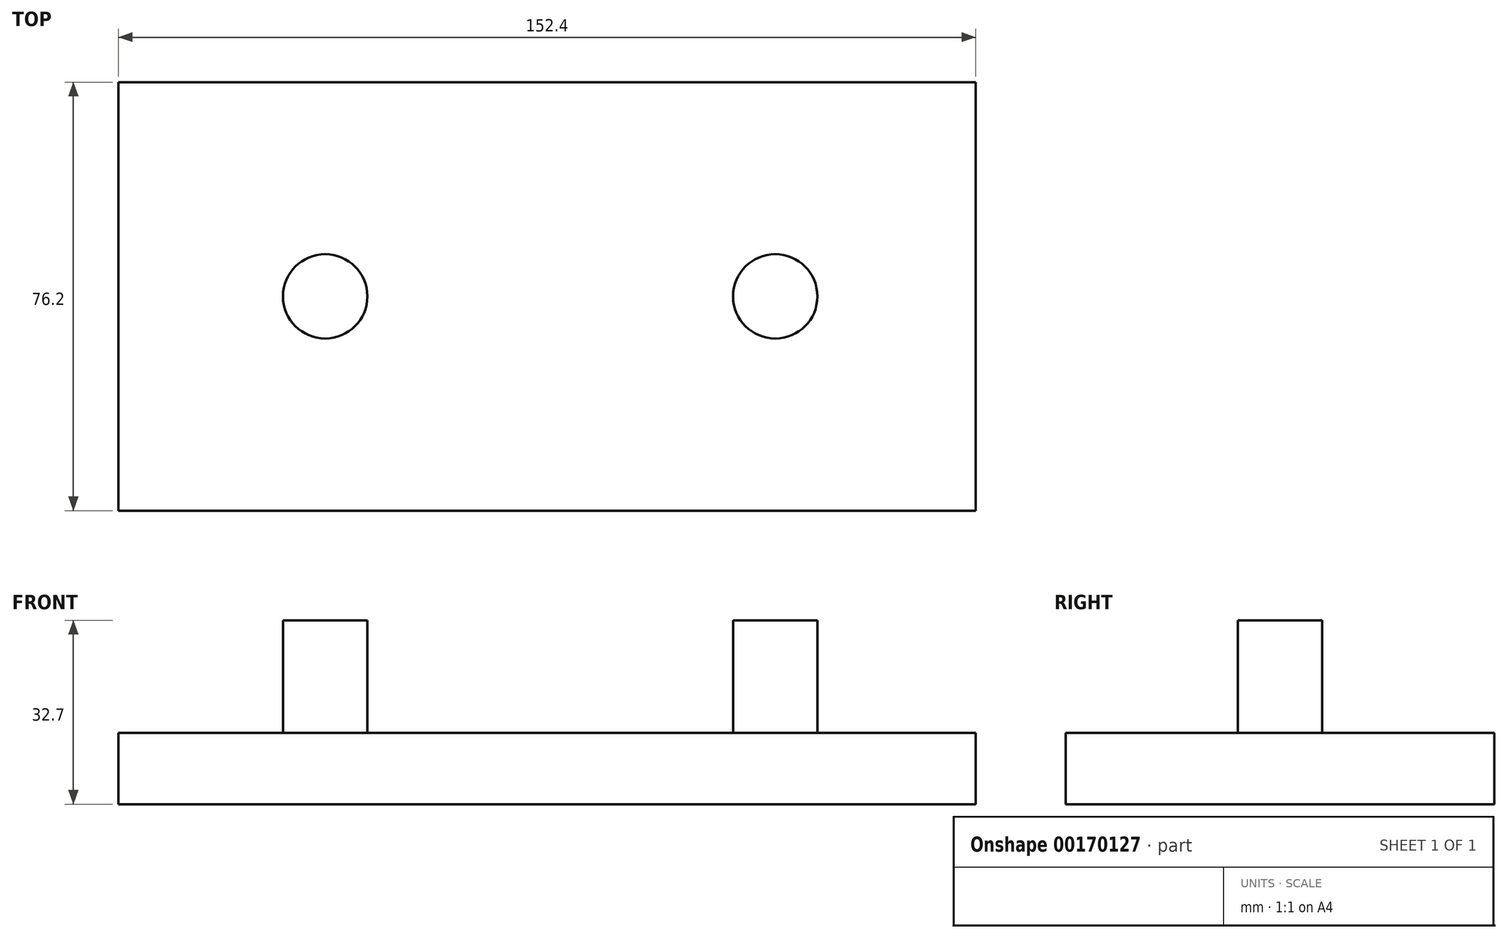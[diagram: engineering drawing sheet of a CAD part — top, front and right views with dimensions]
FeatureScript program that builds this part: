
annotation { "Feature Type Name" : "Feature", "Feature Type Description" : "" }
export const myFeature = defineFeature(function(context is Context, id is Id, definition is map)
    precondition{}
    {
        {
            var Q0;
            Q0=qCreatedBy(makeId("Top.planeOp"),FACE);
            var sketch = newSketch(context, id + "F0", { "sketchPlane" : qUnion([Q0])});
            skLineSegment(sketch, "E0.bottom", {"start": v(-76.2, 38.1) * mm, "end": v(76.2, 38.1) * mm});
            skLineSegment(sketch, "E0.top", {"start": v(-76.2, -38.1) * mm, "end": v(76.2, -38.1) * mm});
            skLineSegment(sketch, "E0.left", {"start": v(-76.2, 38.1) * mm, "end": v(-76.2, -38.1) * mm});
            skLineSegment(sketch, "E0.right", {"start": v(76.2, 38.1) * mm, "end": v(76.2, -38.1) * mm});
            skLineSegment(sketch, "E1", {"start": v(0, 78.25) * mm, "end": v(0, -63.99) * mm, "construction": true});
            skLineSegment(sketch, "E2", {"start": v(-88.68, 0) * mm, "end": v(93.3, 0) * mm, "construction": true});
            skSolve(sketch);
        }
        {
            var Q0;
            Q0=makeQuery(id+"F0.imprint","IMPRINT",FACE,{"disambiguationData":[TD([[makeQuery(id+"F0.imprint","IMPRINT",EDGE,{"derivedFrom":sQuery(id+"F0.wireOp",EDGE,"E0.bottom")}),-1.0]])]});
            extrude(context, id + "F1", {"entities" : qUnion([Q0]), "depth" : 12.7 * mm});
        }
        {
            var Q0;
            Q0=makeQuery(id+"F1.opExtrude","CAP_FACE",FACE,{"disambiguationData":[OSD([sQuery(id+"F0.wireOp",EDGE,"E0.bottom"),sQuery(id+"F0.wireOp",EDGE,"E0.top"),sQuery(id+"F0.wireOp",EDGE,"E0.left"),sQuery(id+"F0.wireOp",EDGE,"E0.right")])],"isStart":false});
            var sketch = newSketch(context, id + "F2", { "sketchPlane" : qUnion([Q0])});
            skCircle(sketch, "E3", {"center": v(-39.44, 0) * mm, "radius": 7.5 * mm});
            skCircle(sketch, "E4", {"center": v(40.56, 0) * mm, "radius": 7.5 * mm});
            skSolve(sketch);
        }
        {
            var Q0;
            Q0=makeQuery(id+"F2.imprint","IMPRINT",FACE,{"disambiguationData":[TD([[makeQuery(id+"F2.imprint","IMPRINT",EDGE,{"derivedFrom":sQuery(id+"F2.wireOp",EDGE,"E3")}),1.0]])]});
            var Q1;
            Q1=makeQuery(id+"F2.imprint","IMPRINT",FACE,{"disambiguationData":[TD([[makeQuery(id+"F2.imprint","IMPRINT",EDGE,{"derivedFrom":sQuery(id+"F2.wireOp",EDGE,"E4")}),1.0]])]});
            extrude(context, id + "F3", {"entities" : qUnion([Q0, Q1]), "operationType" : NewBodyOperationType.ADD, "depth" : 20 * mm});
        }
    });
